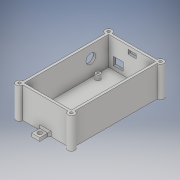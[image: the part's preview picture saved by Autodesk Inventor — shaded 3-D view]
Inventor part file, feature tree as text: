
AUTODESK INVENTOR PART (.ipt)
format: ipt  version: 2019 (Build 230136000, 136)  size: 260,608 bytes
history: native  units: mm
features: extrude x10, sketch x10, projected_geometry x4, mirror x3, chamfer x2
ambient origin geometry x8: Origin, YZ Plane, XZ Plane, XY Plane, X Axis, Y Axis, Z Axis, Center Point
bodies: Solid1 (feature_tree)
feature tree (29):
  extrude  "Extrusion1"  Depth=110.0mm
  extrude  "Extrusion2"  Depth=3.0mm
  extrude  "Extrusion3"  Depth=3.0mm
  extrude  "Extrusion4"  Depth=35.0mm TaperAngle=0.0deg
  extrude  "Extrusion5"  Depth=92.0mm
  extrude  "Extrusion6"  Depth=2.5mm
  extrude  "Extrusion7"  Depth=2.5mm
  mirror  "Mirror1"
  mirror  "Mirror2"
  extrude  "Extrusion8"  Depth=5.92mm
  extrude  "Extrusion9"  Depth=6.0mm
  chamfer  "Chamfer1"  Distance=6.0mm
  extrude  "Extrusion10"  Depth=6.0mm
  mirror  "Mirror3"
  chamfer  "Chamfer2"  Distance=6.0mm
  sketch  "Sketch1"  dims[d0=64.0mm d1=110.0mm]
  sketch  "Sketch2"  dims[d2=3.0mm d3=0.0mm d4=3.0mm]
  projected_geometry  "Projected Loop1"
  sketch  "Sketch3"  dims[d5=3.0mm d6=3.0mm]
  sketch  "Sketch4"  dims[d7=3.0mm d8=35.0mm d9=0.0mm]
  sketch  "Sketch5"  dims[d15=46.16mm d16=92.0mm]
  projected_geometry  "Projected Loop2"
  sketch  "Sketch7"  dims[d17=2.5mm d18=2.5mm]
  projected_geometry  "Projected Loop3"
  sketch  "Sketch8"  dims[d19=2.5mm d20=2.5mm]
  sketch  "Sketch9"  dims[d21=79.0mm d22=5.92mm]
  sketch  "Sketch10"  dims[d23=5.92mm d24=6.0mm]
  sketch  "Sketch11"  dims[d25=6.0mm d26=6.0mm d27=6.0mm d28=6.0mm d29=6.0mm d30=6.0mm d31=0.0mm d33=1.5mm d34=10.0mm d35=12.0mm d36=6.0mm d37=0.0mm d38=20.0mm d39=5.0mm d40=10.0mm d41=24.0mm d42=24.0mm d43=6.0mm d44=0.0mm d45=38.0mm d46=0.0mm d47=3.3mm d48=15.0mm d49=0.0mm d50=12.0mm d51=14.0mm d52=90.0deg d53=3.0mm d54=15.0mm d55=0.0mm d56=4.0mm d57=10.0mm d58=22.757359mm d59=22.757359mm d60=12.0mm d61=0.0mm d62=2.0mm d63=2.0mm d64=45.0deg d65=5.2mm d66=5.0mm d67=5.0mm d68=12.0mm d69=0.0mm d70=2.0mm d71=2.0mm d72=45.0deg]
  projected_geometry  "Projected Loop4"
